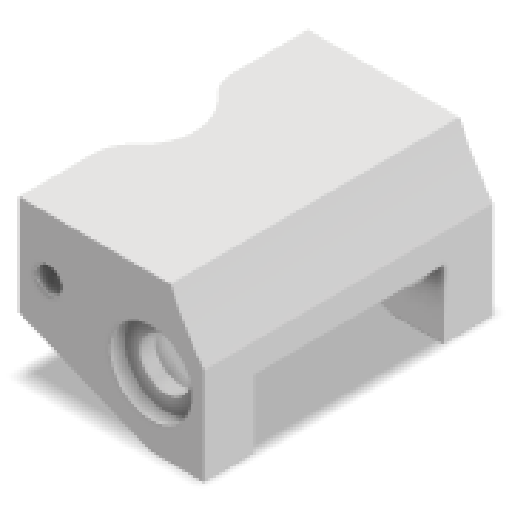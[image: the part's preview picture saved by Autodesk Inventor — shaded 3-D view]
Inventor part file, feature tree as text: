
AUTODESK INVENTOR PART (.ipt)
format: ipt  version: 2025 (Build 290162000, 162)  size: 356,352 bytes
history: native  units: in
note: dims shown in document units (in); Inventor stores cm internally (conversion verified against a paired STEP export)
features: extrude x18, sketch x18, projected_geometry x15, fillet x4, other x3, mirror x2, reference x2, thicken_offset x1, plane x1
ambient origin geometry x8: Origin, YZ Plane, XZ Plane, XY Plane, X Axis, Y Axis, Z Axis, Center Point
bodies: Solid1 (feature_tree)
feature tree (64):
  extrude  "Extrusion1"  Depth=0.25in
  extrude  "Extrusion2"  Depth=2.0in
  extrude  "Extrusion7"  Depth=0.8809in
  extrude  "Extrusion10"  Depth=0.2165in TaperAngle=0.0deg
  extrude  "Extrusion11"  Depth=0.315in
  extrude  "Extrusion12"  TaperAngle=0.0deg  [1 undecoded]
  extrude  "Extrusion13"  Depth=0.3937in TaperAngle=0.0deg
  mirror  "Mirror1"
  fillet  "Fillet5"  Radius=0.3937in
  extrude  "Extrusion14"  Depth=0.3937in
  fillet  "Fillet6"  [1 undecoded]
  extrude  "Extrusion15"  Depth=0.3937in
  thicken_offset  "Thicken1"
  fillet  "Fillet7"  Radius=0.3858in
  extrude  "Extrusion16"  Depth=0.5118in
  extrude  "Extrusion17"  Depth=0.2756in
  extrude  "Extrusion20"  Depth=1.0in TaperAngle=0.0deg
  extrude  "Extrusion21"  Depth=0.315in TaperAngle=0.0deg
  extrude  "Extrusion22"  Depth=0.4724in TaperAngle=0.0deg
  extrude  "Extrusion23"  Depth=0.2047in
  plane  "Work Plane1"
  mirror  "Mirror2"
  fillet  "Fillet9"  [1 undecoded]
  extrude  "Extrusion24"  Depth=0.3543in
  extrude  "Extrusion25"  Depth=0.315in
  extrude  "Extrusion26"  TaperAngle=0.0deg  [1 undecoded]
  sketch  "Sketch1"  dims[d1=1.005in d2=0.25in]
  sketch  "Sketch2"  dims[d3=2.0in d4=0.0in d5=0.5512in]
  projected_geometry  "Projected Loop1"
  sketch  "Sketch7"  dims[d6=0.0in d7=0.0in d21=0.8809in]
  sketch  "Sketch10"  dims[d22=0.1575in d23=0.0in d32=0.2165in d33=0.0in]
  projected_geometry  "Projected Loop7"
  sketch  "Sketch11"  dims[d34=1.1024in d35=0.315in]
  sketch  "Sketch12"  dims[d36=0.2047in d37=0.0in d38=0.0in]
  projected_geometry  "Projected Loop8"
  sketch  "Sketch13"  dims[d39=0.3937in d40=0.0in d42=1.0236in d43=0.0in d45=0.3937in]
  projected_geometry  "Projected Loop9"
  sketch  "Sketch14"  dims[d46=1.0236in d47=0.0in d48=0.3937in d49=0.0in d50=0.0in]
  projected_geometry  "Projected Loop10"
  sketch  "Sketch15"  dims[d51=0.0591in d52=0.1in d53=0.3937in d54=0.3858in]
  projected_geometry  "Projected Loop11"
  sketch  "Sketch16"  dims[d55=0.0079in d56=0.5118in]
  projected_geometry  "Projected Loop12"
  reference  "Reference1"
  sketch  "Sketch17"  dims[d57=0.2756in d58=0.1969in]
  projected_geometry  "Projected Loop13"
  sketch  "Sketch20"  dims[d59=1.0in d60=0.0in d61=1.0in d62=0.0in]
  sketch  "Sketch21"  dims[d71=0.3228in d72=0.315in d73=0.0in]
  sketch  "Sketch22"  dims[d74=0.2756in d75=0.4724in d76=0.0in]
  reference  "Reference3"
  sketch  "Sketch23"  dims[d77=0.2047in d78=0.2047in d79=0.0in d80=0.0in]
  projected_geometry  "Projected Loop15"
  sketch  "Sketch24"  dims[d81=0.3543in d82=0.3543in]
  projected_geometry  "Projected Loop16"
  projected_geometry  "Projected Loop17"
  sketch  "Sketch25"  dims[d83=0.315in d84=0.0in d85=0.7874in]
  projected_geometry  "Projected Loop18"
  sketch  "Sketch26"  dims[d88=0.1969in d89=0.0in d90=0.0in d91=0.0in d100=0.0in d101=0.0in d24=0.0344in d27=0.0in d28=0.0in d29=0.0in d30=0.0in d87=0.0in]
  projected_geometry  "Projected Loop19"
  projected_geometry  "Projected Loop20"
  projected_geometry  "Projected Loop21"
  other  "<userpath>\Desktop\puppycat\singleSwingarmV2.iam"
  other  "singleSwingarmV2.iam"
  other  "trackBase:1"
note: 4 required parameter values undecoded (feature->parameter linkage not recoverable at this tier; creation-order binding heuristic only, values carry confidence <= 0.55)
